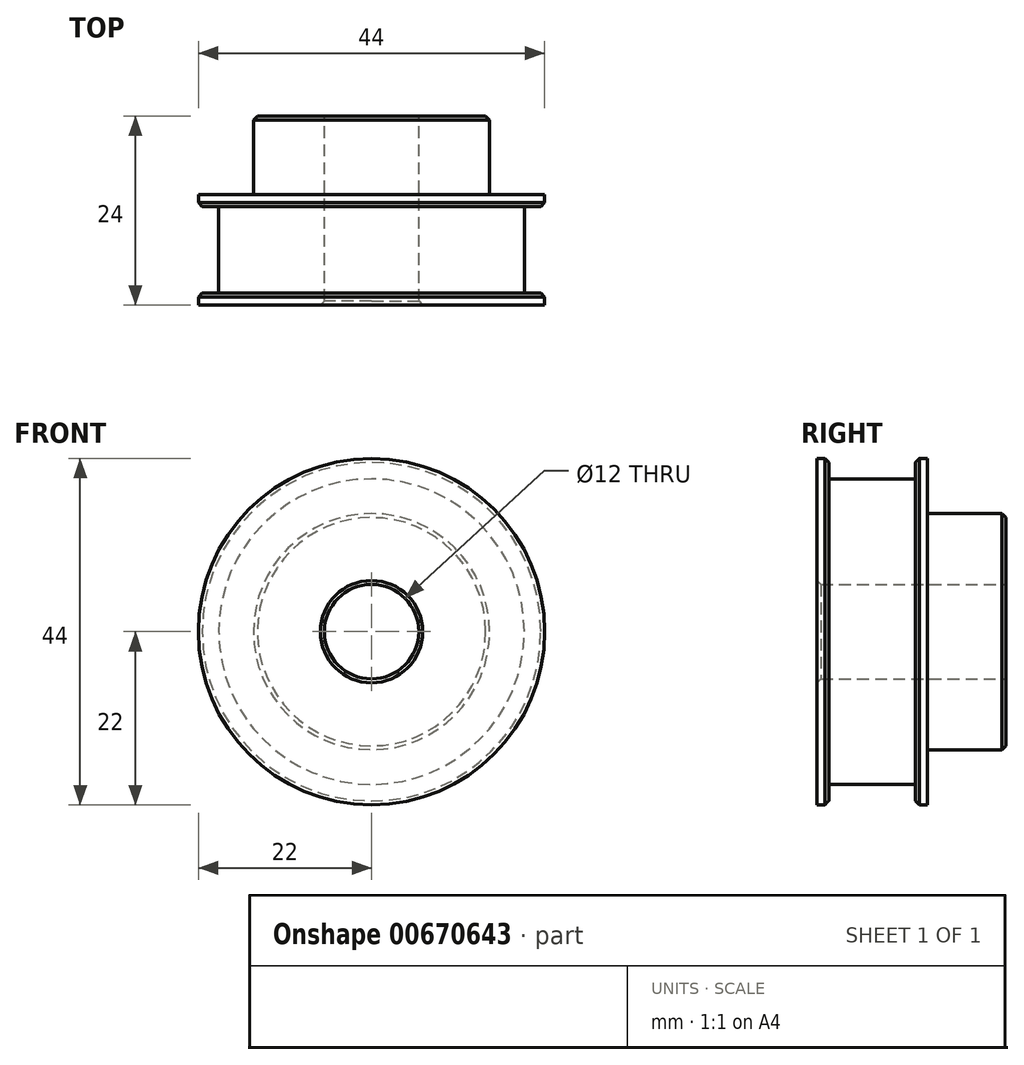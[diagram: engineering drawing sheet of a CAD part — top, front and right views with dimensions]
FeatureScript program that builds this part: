
annotation { "Feature Type Name" : "Feature", "Feature Type Description" : "" }
export const myFeature = defineFeature(function(context is Context, id is Id, definition is map)
    precondition{}
    {
        {
            var Q0;
            Q0=qCreatedBy(makeId("Front.planeOp"),FACE);
            var sketch = newSketch(context, id + "F0", { "sketchPlane" : qUnion([Q0])});
            skCircle(sketch, "E0", {"center": v(0, 0) * mm, "radius": 19.4 * mm});
            skSolve(sketch);
        }
        {
            var Q0;
            Q0=makeQuery(id+"F0.imprint","IMPRINT",FACE,{"disambiguationData":[TD([[makeQuery(id+"F0.imprint","IMPRINT",EDGE,{"derivedFrom":sQuery(id+"F0.wireOp",EDGE,"E0")}),1.0]])]});
            extrude(context, id + "F1", {"entities" : qUnion([Q0]), "endBound" : BoundingType.SYMMETRIC, "depth" : 11 * mm, "offsetDistance" : 25 * mm});
        }
        {
            var Q0;
            Q0=makeQuery(id+"F1.opExtrude","CAP_FACE",FACE,{"disambiguationData":[OSD([sQuery(id+"F0.wireOp",EDGE,"E0")])],"isStart":false});
            var sketch = newSketch(context, id + "F2", { "sketchPlane" : qUnion([Q0])});
            skCircle(sketch, "E1", {"center": v(0, 0) * mm, "radius": 22 * mm});
            skSolve(sketch);
        }
        {
            var Q0;
            Q0 = qSketchRegion(id + "F2", true);
            extrude(context, id + "F3", {"entities" : qUnion([Q0]), "operationType" : NewBodyOperationType.ADD, "depth" : 1.5 * mm, "offsetDistance" : 25 * mm});
        }
        {
            var Q0;
            Q0=makeQuery(id+"F1.opExtrude","CAP_FACE",FACE,{"disambiguationData":[OSD([sQuery(id+"F0.wireOp",EDGE,"E0")])],"isStart":true});
            var sketch = newSketch(context, id + "F4", { "sketchPlane" : qUnion([Q0])});
            skCircle(sketch, "E2", {"center": v(0, 0) * mm, "radius": 22 * mm});
            skSolve(sketch);
        }
        {
            var Q0;
            Q0 = qSketchRegion(id + "F4", true);
            extrude(context, id + "F5", {"entities" : qUnion([Q0]), "operationType" : NewBodyOperationType.ADD, "depth" : 1.5 * mm, "offsetDistance" : 25 * mm});
        }
        {
            var Q0;
            Q0=makeQuery(id+"F5.opExtrude","CAP_FACE",FACE,{"disambiguationData":[OSD([sQuery(id+"F4.wireOp",EDGE,"E2")])],"isStart":false});
            var sketch = newSketch(context, id + "F6", { "sketchPlane" : qUnion([Q0])});
            skCircle(sketch, "E3", {"center": v(0, 0) * mm, "radius": 15 * mm});
            skSolve(sketch);
        }
        {
            var Q0;
            Q0 = qSketchRegion(id + "F6", true);
            extrude(context, id + "F7", {"entities" : qUnion([Q0]), "operationType" : NewBodyOperationType.ADD, "depth" : 10 * mm, "offsetDistance" : 25 * mm});
        }
        {
            var Q0;
            Q0=makeQuery(id+"F7.opExtrude","CAP_FACE",FACE,{"disambiguationData":[OSD([sQuery(id+"F6.wireOp",EDGE,"E3")])],"isStart":false});
            var sketch = newSketch(context, id + "F8", { "sketchPlane" : qUnion([Q0])});
            skCircle(sketch, "E4", {"center": v(0, 0) * mm, "radius": 6 * mm});
            skSolve(sketch);
        }
        {
            var Q0;
            Q0 = qSketchRegion(id + "F8", true);
            extrude(context, id + "F9", {"entities" : qUnion([Q0]), "operationType" : NewBodyOperationType.REMOVE, "endBound" : BoundingType.THROUGH_ALL, "oppositeDirection" : true, "depth" : 25 * mm, "offsetDistance" : 25 * mm});
        }
        {
            var Q0;
            Q0=makeQuery(id+"F9.boolean.opBoolean","INTERSECT",EDGE,{"derivedFrom":[makeQuery(id+"F3.opExtrude","CAP_FACE",FACE,{"disambiguationData":[OSD([sQuery(id+"F2.wireOp",EDGE,"E1")])],"isStart":false}),makeQuery(id+"F9.opExtrude","SWEPT_FACE",FACE,{"disambiguationData":[OSD([sQuery(id+"F8.wireOp",EDGE,"E4")])]})]});
            var Q1;
            Q1=makeQuery(id+"F9.boolean.opBoolean","COPY",EDGE,{"derivedFrom":makeQuery(id+"F9.opExtrude","CAP_EDGE",EDGE,{"disambiguationData":[OSD([sQuery(id+"F8.wireOp",EDGE,"E4")])],"isStart":true})});
            var Q2;
            Q2=makeQuery(id+"F3.opExtrude","CAP_EDGE",EDGE,{"disambiguationData":[OSD([sQuery(id+"F2.wireOp",EDGE,"E1")])],"isStart":true});
            var Q3;
            Q3=makeQuery(id+"F5.opExtrude","CAP_EDGE",EDGE,{"disambiguationData":[OSD([sQuery(id+"F4.wireOp",EDGE,"E2")])],"isStart":true});
            var Q4;
            Q4=makeQuery(id+"F7.opExtrude","CAP_EDGE",EDGE,{"disambiguationData":[OSD([sQuery(id+"F6.wireOp",EDGE,"E3")])],"isStart":false});
            chamfer(context, id + "F10", {"entities" : qUnion([Q0, Q1, Q2, Q3, Q4]), "width" : 0.5 * mm, "tangentPropagation" : true});
        }
    });
